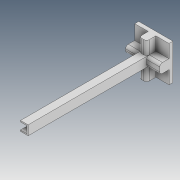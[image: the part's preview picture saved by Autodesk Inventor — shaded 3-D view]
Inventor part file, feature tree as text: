
AUTODESK INVENTOR PART (.ipt)
format: ipt  version: 2021 (Build 250183000, 183)  size: 182,272 bytes
history: native  units: in
note: dims shown in document units (in); Inventor stores cm internally (conversion verified against a paired STEP export)
features: sketch x8, extrude x7, fillet x2, other x1
ambient origin geometry x8: Origin, YZ Plane, XZ Plane, XY Plane, X Axis, Y Axis, Z Axis, Center Point
bodies: Body1 (feature_tree)
feature tree (18):
  other  "Sólido1"
  sketch  "Esboço1"  dims[d0=0.2835in d1=0.0394in]
  extrude  "Extrusão1"  Depth=0.0394in
  extrude  "Extrusão2"  Depth=0.187in
  extrude  "Extrusão3"  Depth=3.937in TaperAngle=0.0deg
  extrude  "Extrusão4"  Depth=0.3937in TaperAngle=0.0deg
  extrude  "Extrusão5"  Depth=0.3937in TaperAngle=0.0deg
  fillet  "Arredondamento1"  Radius=0.1181in
  extrude  "Extrusão6"  Depth=0.0787in
  extrude  "Extrusão7"  Depth=0.4035in TaperAngle=0.0deg
  fillet  "Arredondamento2"  Radius=0.0787in
  sketch  "Esboço2"  dims[d2=0.2264in d3=0.187in]
  sketch  "Esboço3"  dims[d4=0.2047in d5=3.937in d6=0.0in]
  sketch  "Esboço4"  dims[d7=0.3937in d8=0.3937in d9=0.0in]
  sketch  "Esboço5"  dims[d10=0.3937in d11=0.0in d12=0.3937in d13=0.0in d14=0.1181in]
  sketch  "Esboço6"  dims[d15=0.3937in d16=0.0in d17=0.0787in]
  sketch  "Esboço7"  dims[d18=0.5906in d19=0.0in d20=0.4035in d21=0.0in d22=0.0787in]
  sketch  "Esboço8"
